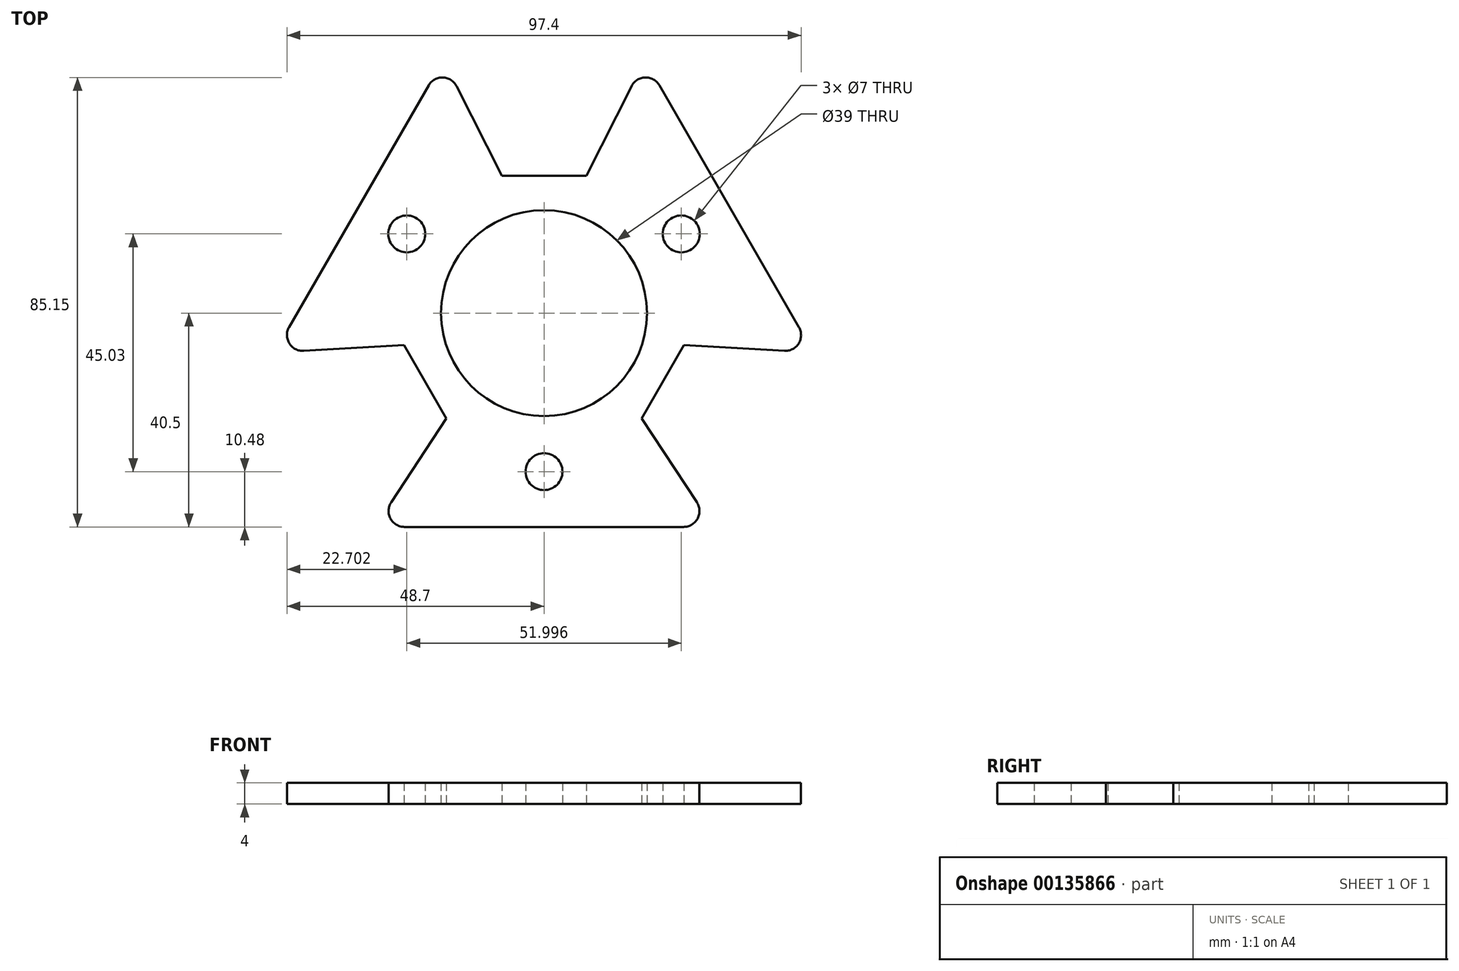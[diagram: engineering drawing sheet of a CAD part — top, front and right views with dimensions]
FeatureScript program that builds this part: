
annotation { "Feature Type Name" : "Feature", "Feature Type Description" : "" }
export const myFeature = defineFeature(function(context is Context, id is Id, definition is map)
    precondition{}
    {
        {
            var Q0;
            Q0=qCreatedBy(makeId("Top.planeOp"),FACE);
            var sketch = newSketch(context, id + "F0", { "sketchPlane" : qUnion([Q0])});
            skLineSegment(sketch, "E0.0.0", {"start": v(-19.07, 47.96) * mm, "end": v(-51.07, -7.46) * mm});
            skLineSegment(sketch, "E0.0.3", {"start": v(-26.52, -6.07) * mm, "end": v(-18.52, -19.93) * mm});
            skLineSegment(sketch, "E0.0.6", {"start": v(-32, -40.5) * mm, "end": v(32, -40.5) * mm});
            skLineSegment(sketch, "E0.0.9", {"start": v(18.52, -19.93) * mm, "end": v(26.52, -6.07) * mm});
            skLineSegment(sketch, "E0.0.12", {"start": v(51.07, -7.46) * mm, "end": v(19.07, 47.96) * mm});
            skLineSegment(sketch, "E0.0.15", {"start": v(8, 26) * mm, "end": v(-8, 26) * mm});
            skCircle(sketch, "E1.0", {"center": v(0, -30.02) * mm, "radius": 3.9 * mm, "construction": true});
            skCircle(sketch, "E2.0", {"center": v(0, 0) * mm, "radius": 19.5 * mm});
            skCircle(sketch, "E3", {"center": v(0, 0) * mm, "radius": 26 * mm, "construction": true});
            skCircle(sketch, "E4", {"center": v(0, 0) * mm, "radius": 40.5 * mm, "construction": true});
            skCircle(sketch, "E5", {"center": v(-26, 15.01) * mm, "radius": 3.5 * mm});
            skCircle(sketch, "E6", {"center": v(26, 15.01) * mm, "radius": 3.5 * mm});
            skCircle(sketch, "E7", {"center": v(0, -30.02) * mm, "radius": 3.5 * mm});
            skLineSegment(sketch, "E8", {"start": v(-19.07, 47.96) * mm, "end": v(-8, 26) * mm});
            skLineSegment(sketch, "E9", {"start": v(8, 26) * mm, "end": v(19.07, 47.96) * mm});
            skLineSegment(sketch, "E10", {"start": v(26.52, -6.07) * mm, "end": v(51.07, -7.46) * mm});
            skLineSegment(sketch, "E11", {"start": v(32, -40.5) * mm, "end": v(18.52, -19.93) * mm});
            skLineSegment(sketch, "E12", {"start": v(-32, -40.5) * mm, "end": v(-18.52, -19.93) * mm});
            skLineSegment(sketch, "E13", {"start": v(-51.07, -7.46) * mm, "end": v(-26.52, -6.07) * mm});
            skPoint(sketch, "E14", {"position": v(22.52, -13) * mm});
            skPoint(sketch, "E15", {"position": v(-22.52, -13) * mm});
            skPoint(sketch, "E16", {"position": v(0, 26) * mm});
            skPoint(sketch, "E17", {"position": v(35.07, 20.25) * mm});
            skPoint(sketch, "E18", {"position": v(0, -40.5) * mm});
            skPoint(sketch, "E19", {"position": v(-35.07, 20.25) * mm});
            skCircle(sketch, "E20.cCircle", {"center": v(0, 0) * mm, "radius": 30.02 * mm, "construction": true});
            skLineSegment(sketch, "E20.0", {"start": v(-26, 15.01) * mm, "end": v(26, 15.01) * mm, "construction": true});
            skLineSegment(sketch, "E20.1", {"start": v(26, 15.01) * mm, "end": v(0, -30.02) * mm, "construction": true});
            skLineSegment(sketch, "E20.2", {"start": v(0, -30.02) * mm, "end": v(-26, 15) * mm, "construction": true});
            skSolve(sketch);
        }
        {
            var Q0;
            Q0 = qSketchRegion(id + "F0", true);
            extrude(context, id + "F1", {"entities" : qUnion([Q0]), "endBound" : BoundingType.SYMMETRIC, "depth" : 4 * mm});
        }
        {
            var Q0;
            Q0=makeQuery(id+"F1.opExtrude","SWEPT_EDGE",EDGE,{"disambiguationData":[OSD([sQuery(id+"F0.wireOp",EDGE,"E0.0.12"),sQuery(id+"F0.wireOp",EDGE,"E10")])]});
            var Q1;
            Q1=makeQuery(id+"F1.opExtrude","SWEPT_EDGE",EDGE,{"disambiguationData":[OSD([sQuery(id+"F0.wireOp",EDGE,"E0.0.6"),sQuery(id+"F0.wireOp",EDGE,"E11")])]});
            var Q2;
            Q2=makeQuery(id+"F1.opExtrude","SWEPT_EDGE",EDGE,{"disambiguationData":[OSD([sQuery(id+"F0.wireOp",EDGE,"E0.0.0"),sQuery(id+"F0.wireOp",EDGE,"E8")])]});
            var Q3;
            Q3=makeQuery(id+"F1.opExtrude","SWEPT_EDGE",EDGE,{"disambiguationData":[OSD([sQuery(id+"F0.wireOp",EDGE,"E0.0.12"),sQuery(id+"F0.wireOp",EDGE,"E9")])]});
            var Q4;
            Q4=makeQuery(id+"F1.opExtrude","SWEPT_EDGE",EDGE,{"disambiguationData":[OSD([sQuery(id+"F0.wireOp",EDGE,"E0.0.0"),sQuery(id+"F0.wireOp",EDGE,"E13")])]});
            var Q5;
            Q5=makeQuery(id+"F1.opExtrude","SWEPT_EDGE",EDGE,{"disambiguationData":[OSD([sQuery(id+"F0.wireOp",EDGE,"E0.0.6"),sQuery(id+"F0.wireOp",EDGE,"E12")])]});
            fillet(context, id + "F2", {"entities" : qUnion([Q0, Q1, Q2, Q3, Q4, Q5]), "radius" : 3 * mm, "tangentPropagation" : true, "allowEdgeOverflow" : false});
        }
    });
